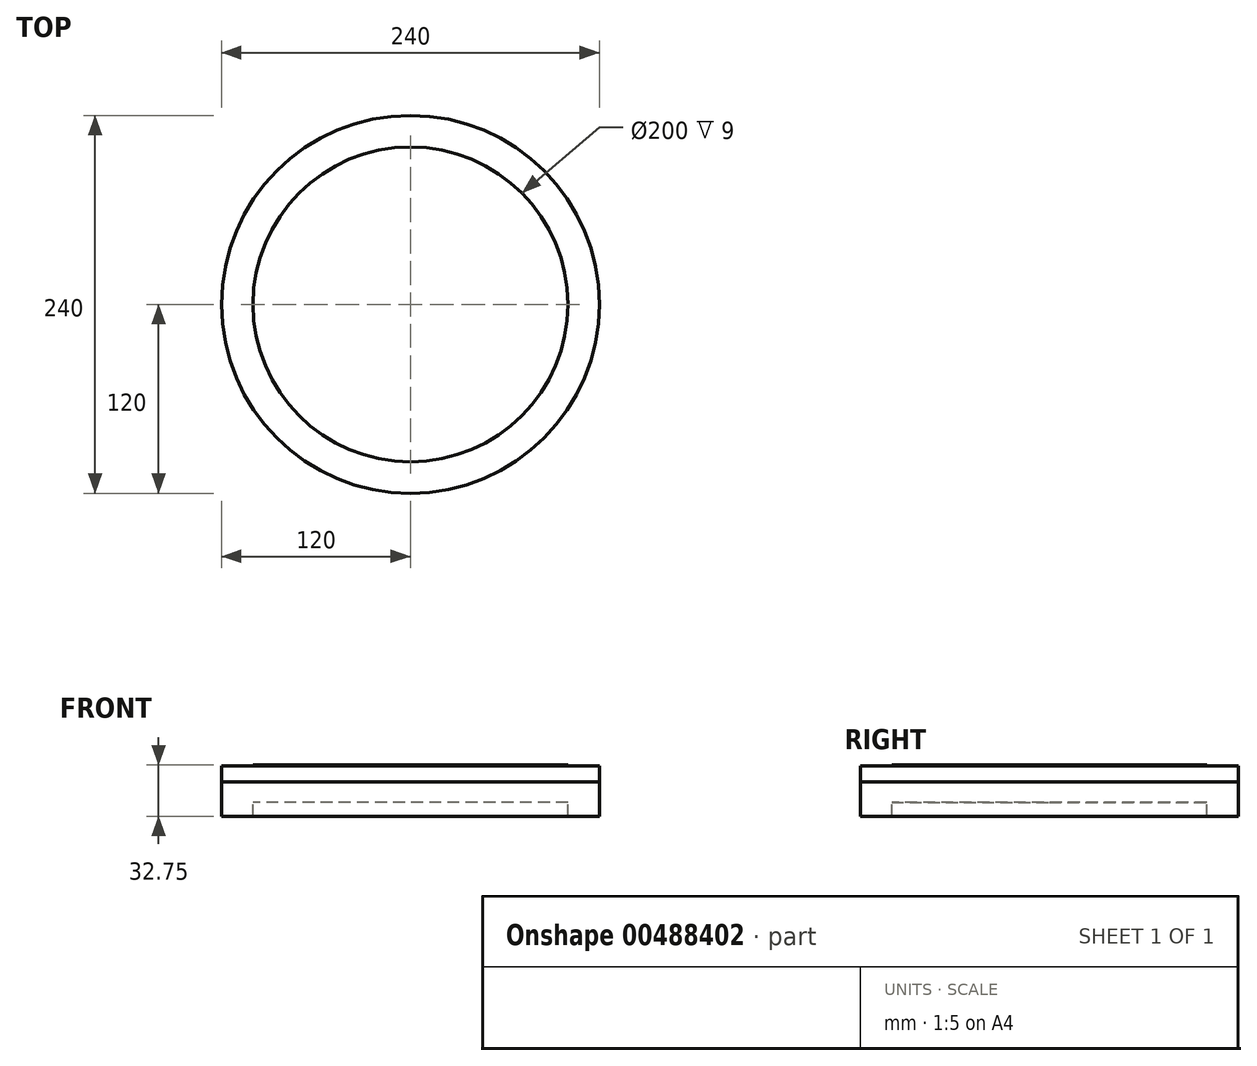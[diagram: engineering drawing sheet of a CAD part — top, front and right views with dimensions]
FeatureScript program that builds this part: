
annotation { "Feature Type Name" : "Feature", "Feature Type Description" : "" }
export const myFeature = defineFeature(function(context is Context, id is Id, definition is map)
    precondition{}
    {
        {
            var Q0;
            Q0=qCreatedBy(makeId("Top.planeOp"),FACE);
            var sketch = newSketch(context, id + "F0", { "sketchPlane" : qUnion([Q0])});
            skCircle(sketch, "E0", {"center": v(0, 0) * mm, "radius": 120 * mm});
            skCircle(sketch, "E1", {"center": v(0, 0) * mm, "radius": 100 * mm});
            skSolve(sketch);
        }
        {
            var Q0;
            Q0=makeQuery(id+"F0.imprint","IMPRINT",FACE,{"disambiguationData":[TD([[makeQuery(id+"F0.imprint","IMPRINT",EDGE,{"derivedFrom":sQuery(id+"F0.wireOp",EDGE,"E0")}),1.0]])]});
            extrude(context, id + "F1", {"entities" : qUnion([Q0]), "oppositeDirection" : true, "depth" : 9 * mm});
        }
        {
            var Q0;
            Q0=makeQuery(id+"F0.imprint","IMPRINT",FACE,{"disambiguationData":[TD([[makeQuery(id+"F0.imprint","IMPRINT",EDGE,{"derivedFrom":sQuery(id+"F0.wireOp",EDGE,"E1")}),1.0]])]});
            extrude(context, id + "F2", {"entities" : qUnion([Q0]), "depth" : 4 * mm});
        }
        {
            var Q0;
            Q0=makeQuery(id+"F0.imprint","IMPRINT",FACE,{"disambiguationData":[TD([[makeQuery(id+"F0.imprint","IMPRINT",EDGE,{"derivedFrom":sQuery(id+"F0.wireOp",EDGE,"E0")}),1.0]])]});
            extrude(context, id + "F3", {"entities" : qUnion([Q0]), "operationType" : NewBodyOperationType.ADD, "depth" : 13 * mm});
        }
        {
            var Q0;
            Q0=makeQuery(id+"F2.opExtrude","CAP_FACE",FACE,{"disambiguationData":[OSD([sQuery(id+"F0.wireOp",EDGE,"E1")])],"isStart":false});
            extrude(context, id + "F4", {"entities" : qUnion([Q0]), "operationType" : NewBodyOperationType.ADD, "depth" : 9 * mm});
        }
        {
            var Q0;
            {var subQ0=sQuery(id+"F0.wireOp",EDGE,"E1");Q0=makeQuery(id+"F4.boolean.opBoolean","MERGE",FACE,{"derivedFrom":[makeQuery(id+"F3.opExtrude","CAP_FACE",FACE,{"disambiguationData":[OSD([sQuery(id+"F0.wireOp",EDGE,"E0"),subQ0])],"isStart":false}),makeQuery(id+"F4.opExtrude","CAP_FACE",FACE,{"disambiguationData":[OSD([subQ0])],"isStart":false})]});}
            extrude(context, id + "F5", {"entities" : qUnion([Q0]), "depth" : 10 * mm});
        }
        {
            var Q0;
            Q0=makeQuery(id+"F5.opExtrude","CAP_FACE",FACE,{"disambiguationData":[OSD([sQuery(id+"F0.wireOp",EDGE,"E0"),sQuery(id+"F0.wireOp",EDGE,"E1")])],"isStart":false});
            var sketch = newSketch(context, id + "F6", { "sketchPlane" : qUnion([Q0])});
            skCircle(sketch, "E2", {"center": v(0, 0) * mm, "radius": 100 * mm});
            skSolve(sketch);
        }
        {
            var Q0;
            Q0=makeQuery(id+"F6.imprint","IMPRINT",FACE,{"disambiguationData":[TD([[makeQuery(id+"F6.imprint","IMPRINT",EDGE,{"derivedFrom":sQuery(id+"F6.wireOp",EDGE,"E2")}),1.0]])]});
            extrude(context, id + "F7", {"entities" : qUnion([Q0]), "depth" : 0.75 * mm});
        }
    });
